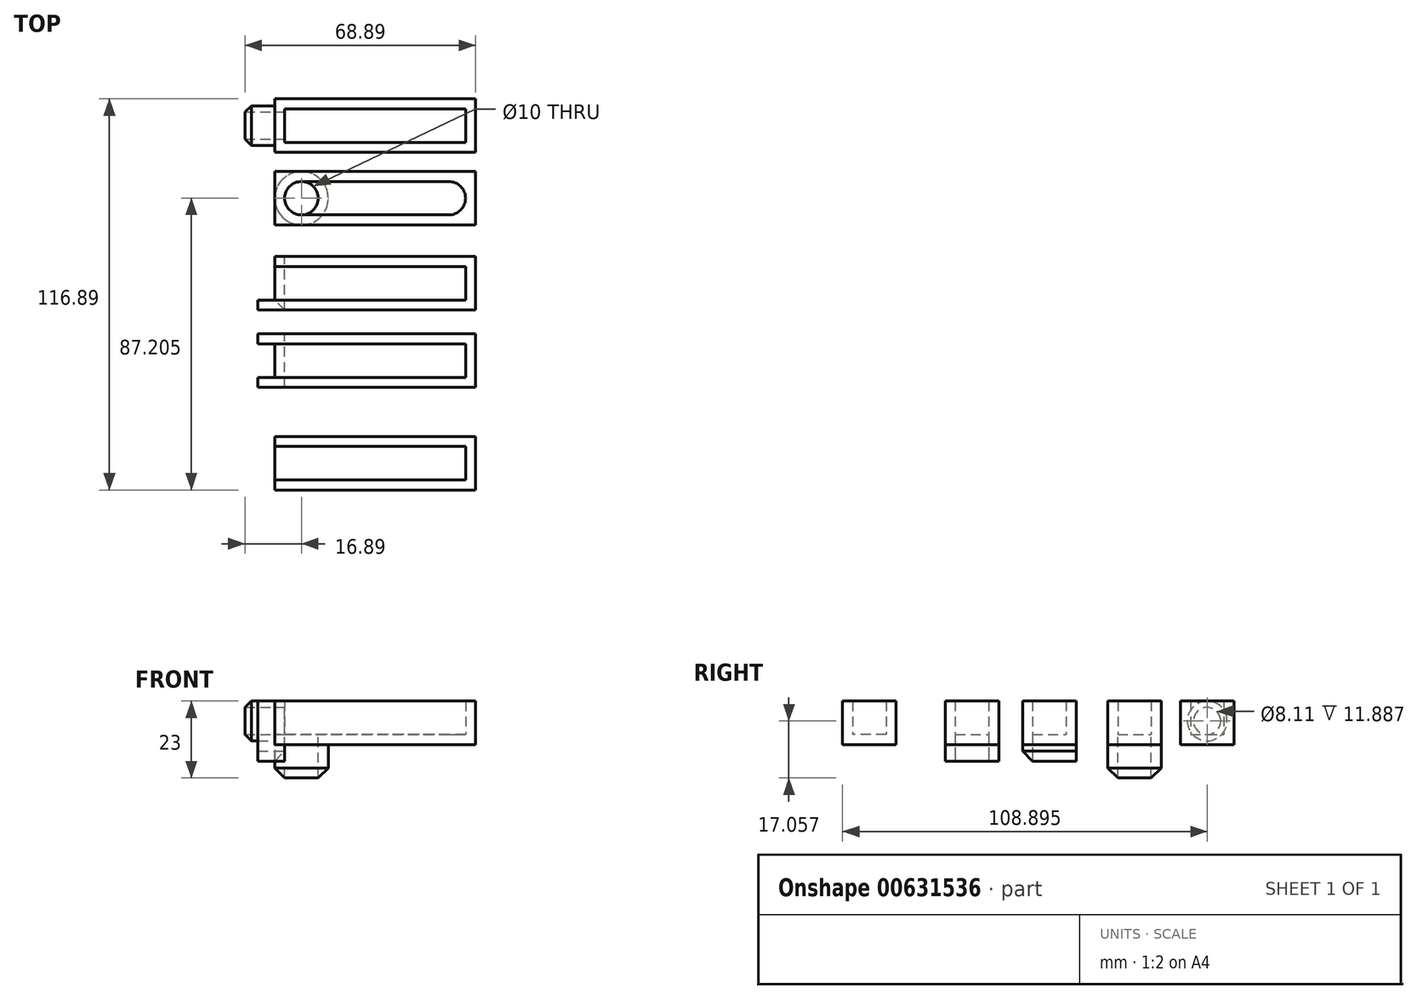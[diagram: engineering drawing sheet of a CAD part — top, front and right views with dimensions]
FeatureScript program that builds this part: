
annotation { "Feature Type Name" : "Feature", "Feature Type Description" : "" }
export const myFeature = defineFeature(function(context is Context, id is Id, definition is map)
    precondition{}
    {
        {
            var Q0;
            Q0=qCreatedBy(makeId("Top.planeOp"),FACE);
            var sketch = newSketch(context, id + "F0", { "sketchPlane" : qUnion([Q0])});
            skLineSegment(sketch, "E0.bottom", {"start": v(-30, 8) * mm, "end": v(30, 8) * mm});
            skLineSegment(sketch, "E0.top", {"start": v(-30, -8) * mm, "end": v(30, -8) * mm});
            skLineSegment(sketch, "E0.left", {"start": v(-30, 8) * mm, "end": v(-30, -8) * mm});
            skLineSegment(sketch, "E0.right", {"start": v(30, 8) * mm, "end": v(30, -8) * mm});
            skPoint(sketch, "E0.middle", {"position": v(0, 0) * mm});
            skLineSegment(sketch, "E1", {"start": v(-30, 5) * mm, "end": v(27, 5) * mm});
            skLineSegment(sketch, "E2", {"start": v(27, 5) * mm, "end": v(27, -5) * mm});
            skLineSegment(sketch, "E3", {"start": v(27, -5) * mm, "end": v(-30, -5) * mm});
            skLineSegment(sketch, "E4.bottom", {"start": v(-30, 22.66) * mm, "end": v(30, 22.66) * mm});
            skLineSegment(sketch, "E4.top", {"start": v(-30, 38.66) * mm, "end": v(30, 38.66) * mm});
            skLineSegment(sketch, "E4.left", {"start": v(-30, 22.66) * mm, "end": v(-30, 38.66) * mm});
            skLineSegment(sketch, "E4.right", {"start": v(30, 22.66) * mm, "end": v(30, 38.66) * mm});
            skLineSegment(sketch, "E5.bottom", {"start": v(-30, 45.78) * mm, "end": v(30, 45.78) * mm});
            skLineSegment(sketch, "E5.top", {"start": v(-30, 61.78) * mm, "end": v(30, 61.78) * mm});
            skLineSegment(sketch, "E5.left", {"start": v(-30, 45.78) * mm, "end": v(-30, 61.78) * mm});
            skLineSegment(sketch, "E5.right", {"start": v(30, 45.78) * mm, "end": v(30, 61.78) * mm});
            skLineSegment(sketch, "E6.bottom", {"start": v(27, 35.66) * mm, "end": v(-30, 35.66) * mm});
            skLineSegment(sketch, "E6.top", {"start": v(27, 25.66) * mm, "end": v(-30, 25.66) * mm});
            skLineSegment(sketch, "E6.left", {"start": v(27, 35.66) * mm, "end": v(27, 25.66) * mm});
            skLineSegment(sketch, "E6.right", {"start": v(-30, 35.66) * mm, "end": v(-30, 25.66) * mm});
            skLineSegment(sketch, "E7.bottom", {"start": v(27, 58.78) * mm, "end": v(-30, 58.78) * mm});
            skLineSegment(sketch, "E7.top", {"start": v(27, 48.78) * mm, "end": v(-30, 48.78) * mm});
            skLineSegment(sketch, "E7.left", {"start": v(27, 58.78) * mm, "end": v(27, 48.78) * mm});
            skLineSegment(sketch, "E7.right", {"start": v(-30, 58.78) * mm, "end": v(-30, 48.78) * mm});
            skLineSegment(sketch, "E8.bottom", {"start": v(-30, 71.2) * mm, "end": v(30, 71.2) * mm});
            skLineSegment(sketch, "E8.top", {"start": v(-30, 87.2) * mm, "end": v(30, 87.2) * mm});
            skLineSegment(sketch, "E8.left", {"start": v(-30, 71.2) * mm, "end": v(-30, 87.2) * mm});
            skLineSegment(sketch, "E8.right", {"start": v(30, 71.2) * mm, "end": v(30, 87.2) * mm});
            skLineSegment(sketch, "E9.bottom", {"start": v(-30, 92.9) * mm, "end": v(30, 92.9) * mm});
            skLineSegment(sketch, "E9.top", {"start": v(-30, 108.9) * mm, "end": v(30, 108.9) * mm});
            skLineSegment(sketch, "E9.left", {"start": v(-30, 92.9) * mm, "end": v(-30, 108.9) * mm});
            skLineSegment(sketch, "E9.right", {"start": v(30, 92.9) * mm, "end": v(30, 108.9) * mm});
            skLineSegment(sketch, "E10.bottom", {"start": v(22, 84.2) * mm, "end": v(-22, 84.2) * mm});
            skLineSegment(sketch, "E10.top", {"start": v(22, 74.2) * mm, "end": v(-22, 74.2) * mm});
            skLineSegment(sketch, "E10.left", {"start": v(27, 79.2) * mm, "end": v(27, 79.2) * mm});
            skLineSegment(sketch, "E10.right", {"start": v(-27, 79.2) * mm, "end": v(-27, 79.2) * mm});
            skLineSegment(sketch, "E11.bottom", {"start": v(-27, 95.9) * mm, "end": v(27, 95.9) * mm});
            skLineSegment(sketch, "E11.top", {"start": v(-27, 105.9) * mm, "end": v(27, 105.9) * mm});
            skLineSegment(sketch, "E11.left", {"start": v(-27, 95.9) * mm, "end": v(-27, 105.9) * mm});
            skLineSegment(sketch, "E11.right", {"start": v(27, 95.9) * mm, "end": v(27, 105.9) * mm});
            skPoint(sketch, "E12.visualSharp", {"position": v(27, 84.2) * mm});
            skArc(sketch, "E12.filletArc", {"start": v(27, 79.2) * mm, "mid": v(25.54, 82.74) * mm, "end": v(22, 84.2) * mm});
            skPoint(sketch, "E13.visualSharp", {"position": v(27, 74.2) * mm});
            skArc(sketch, "E13.filletArc", {"start": v(22, 74.2) * mm, "mid": v(25.54, 75.67) * mm, "end": v(27, 79.2) * mm});
            skPoint(sketch, "E14.visualSharp", {"position": v(-27, 84.2) * mm});
            skArc(sketch, "E14.filletArc", {"start": v(-22, 84.2) * mm, "mid": v(-25.54, 82.74) * mm, "end": v(-27, 79.2) * mm});
            skPoint(sketch, "E15.visualSharp", {"position": v(-27, 74.2) * mm});
            skArc(sketch, "E15.filletArc", {"start": v(-27, 79.2) * mm, "mid": v(-25.54, 75.67) * mm, "end": v(-22, 74.2) * mm});
            skCircle(sketch, "E16", {"center": v(-22, 79.2) * mm, "radius": 5 * mm});
            skSolve(sketch);
        }
        {
            var Q0;
            {var subQ0=sQuery(id+"F0.wireOp",EDGE,"E1");Q0=makeQuery(id+"F0.imprint","IMPRINT",FACE,{"disambiguationData":[TD([[makeQuery(id+"F0.imprint","IMPRINT",EDGE,{"derivedFrom":subQ0}),-1.0]])]});}
            var Q1;
            {var subQ3=sQuery(id+"F0.wireOp",EDGE,"E0.bottom");Q1=makeQuery(id+"F0.imprint","IMPRINT",FACE,{"disambiguationData":[TD([[makeQuery(id+"F0.imprint","IMPRINT",EDGE,{"derivedFrom":subQ3}),-1.0]])]});}
            var Q2;
            {var subQ4=sQuery(id+"F0.wireOp",EDGE,"E4.bottom");Q2=makeQuery(id+"F0.imprint","IMPRINT",FACE,{"disambiguationData":[TD([[makeQuery(id+"F0.imprint","IMPRINT",EDGE,{"derivedFrom":subQ4}),1.0]])]});}
            var Q3;
            Q3=makeQuery(id+"F0.imprint","IMPRINT",FACE,{"disambiguationData":[TD([[makeQuery(id+"F0.imprint","IMPRINT",EDGE,{"derivedFrom":sQuery(id+"F0.wireOp",EDGE,"E6.bottom")}),1.0]])]});
            var Q4;
            {var subQ4=sQuery(id+"F0.wireOp",EDGE,"E5.bottom");Q4=makeQuery(id+"F0.imprint","IMPRINT",FACE,{"disambiguationData":[TD([[makeQuery(id+"F0.imprint","IMPRINT",EDGE,{"derivedFrom":subQ4}),1.0]])]});}
            var Q5;
            Q5=makeQuery(id+"F0.imprint","IMPRINT",FACE,{"disambiguationData":[TD([[makeQuery(id+"F0.imprint","IMPRINT",EDGE,{"derivedFrom":sQuery(id+"F0.wireOp",EDGE,"E7.bottom")}),1.0]])]});
            var Q6;
            Q6=makeQuery(id+"F0.imprint","IMPRINT",FACE,{"disambiguationData":[TD([[makeQuery(id+"F0.imprint","IMPRINT",EDGE,{"derivedFrom":sQuery(id+"F0.wireOp",EDGE,"E8.bottom")}),1.0]])]});
            var Q7;
            {var subQ1=sQuery(id+"F0.wireOp",EDGE,"E10.bottom");Q7=makeQuery(id+"F0.imprint","IMPRINT",FACE,{"disambiguationData":[TD([[makeQuery(id+"F0.imprint","IMPRINT",EDGE,{"derivedFrom":subQ1}),1.0]])]});}
            var Q8;
            Q8=makeQuery(id+"F0.imprint","IMPRINT",FACE,{"disambiguationData":[TD([[makeQuery(id+"F0.imprint","IMPRINT",EDGE,{"derivedFrom":sQuery(id+"F0.wireOp",EDGE,"E9.bottom")}),1.0]])]});
            var Q9;
            Q9=makeQuery(id+"F0.imprint","IMPRINT",FACE,{"disambiguationData":[TD([[makeQuery(id+"F0.imprint","IMPRINT",EDGE,{"derivedFrom":sQuery(id+"F0.wireOp",EDGE,"E11.bottom")}),1.0]])]});
            extrude(context, id + "F1", {"entities" : qUnion([Q0, Q1, Q2, Q3, Q4, Q5, Q6, Q7, Q8, Q9]), "oppositeDirection" : true, "depth" : 3 * mm, "offsetDistance" : 25 * mm});
        }
        {
            var Q0;
            {var subQ3=sQuery(id+"F0.wireOp",EDGE,"E0.bottom");Q0=makeQuery(id+"F0.imprint","IMPRINT",FACE,{"disambiguationData":[TD([[makeQuery(id+"F0.imprint","IMPRINT",EDGE,{"derivedFrom":subQ3}),-1.0]])]});}
            extrude(context, id + "F2", {"entities" : qUnion([Q0]), "operationType" : NewBodyOperationType.ADD, "depth" : 10 * mm, "offsetDistance" : 25 * mm});
        }
        {
            var Q0;
            {var subQ4=sQuery(id+"F0.wireOp",EDGE,"E4.bottom");Q0=makeQuery(id+"F0.imprint","IMPRINT",FACE,{"disambiguationData":[TD([[makeQuery(id+"F0.imprint","IMPRINT",EDGE,{"derivedFrom":subQ4}),1.0]])]});}
            extrude(context, id + "F3", {"entities" : qUnion([Q0]), "operationType" : NewBodyOperationType.ADD, "depth" : 10 * mm, "offsetDistance" : 25 * mm});
        }
        {
            var Q0;
            {var subQ4=sQuery(id+"F0.wireOp",EDGE,"E5.bottom");Q0=makeQuery(id+"F0.imprint","IMPRINT",FACE,{"disambiguationData":[TD([[makeQuery(id+"F0.imprint","IMPRINT",EDGE,{"derivedFrom":subQ4}),1.0]])]});}
            extrude(context, id + "F4", {"entities" : qUnion([Q0]), "operationType" : NewBodyOperationType.ADD, "depth" : 10 * mm, "offsetDistance" : 25 * mm});
        }
        {
            var Q0;
            Q0=makeQuery(id+"F0.imprint","IMPRINT",FACE,{"disambiguationData":[TD([[makeQuery(id+"F0.imprint","IMPRINT",EDGE,{"derivedFrom":sQuery(id+"F0.wireOp",EDGE,"E8.bottom")}),1.0]])]});
            extrude(context, id + "F5", {"entities" : qUnion([Q0]), "operationType" : NewBodyOperationType.ADD, "depth" : 10 * mm, "offsetDistance" : 25 * mm});
        }
        {
            var Q0;
            Q0=makeQuery(id+"F0.imprint","IMPRINT",FACE,{"disambiguationData":[TD([[makeQuery(id+"F0.imprint","IMPRINT",EDGE,{"derivedFrom":sQuery(id+"F0.wireOp",EDGE,"E9.bottom")}),1.0]])]});
            extrude(context, id + "F6", {"entities" : qUnion([Q0]), "operationType" : NewBodyOperationType.ADD, "depth" : 10 * mm, "offsetDistance" : 25 * mm});
        }
        {
            var Q0;
            Q0=makeQuery(id+"F1.opExtrude","CAP_FACE",FACE,{"disambiguationData":[OSD([sQuery(id+"F0.wireOp",EDGE,"E4.bottom"),sQuery(id+"F0.wireOp",EDGE,"E4.top"),sQuery(id+"F0.wireOp",EDGE,"E4.left"),sQuery(id+"F0.wireOp",EDGE,"E4.right"),sQuery(id+"F0.wireOp",EDGE,"E6.right")])],"isStart":false});
            var sketch = newSketch(context, id + "F7", { "sketchPlane" : qUnion([Q0])});
            skLineSegment(sketch, "E17.0", {"start": v(-30, -22.66) * mm, "end": v(-30, -38.66) * mm});
            skLineSegment(sketch, "E18.0", {"start": v(-30, -45.78) * mm, "end": v(-30, -61.78) * mm});
            skCircle(sketch, "E19.0", {"center": v(-22, -79.2) * mm, "radius": 5 * mm});
            skLineSegment(sketch, "E20.bottom", {"start": v(-30, -22.66) * mm, "end": v(-27, -22.66) * mm});
            skLineSegment(sketch, "E20.top", {"start": v(-30, -38.66) * mm, "end": v(-27, -38.66) * mm});
            skLineSegment(sketch, "E20.right", {"start": v(-27, -22.66) * mm, "end": v(-27, -38.66) * mm});
            skLineSegment(sketch, "E21.bottom", {"start": v(-30, -45.78) * mm, "end": v(-27, -45.78) * mm});
            skLineSegment(sketch, "E21.top", {"start": v(-30, -61.78) * mm, "end": v(-27, -61.78) * mm});
            skLineSegment(sketch, "E21.right", {"start": v(-27, -45.78) * mm, "end": v(-27, -61.78) * mm});
            skCircle(sketch, "E22", {"center": v(-22, -79.2) * mm, "radius": 8 * mm});
            skSolve(sketch);
        }
        {
            var Q0;
            Q0=makeQuery(id+"F7.imprint","IMPRINT",FACE,{"disambiguationData":[TD([[makeQuery(id+"F7.imprint","IMPRINT",EDGE,{"derivedFrom":sQuery(id+"F7.wireOp",EDGE,"E20.bottom")}),-1.0]])]});
            extrude(context, id + "F8", {"entities" : qUnion([Q0]), "operationType" : NewBodyOperationType.ADD, "depth" : 5 * mm, "offsetDistance" : 25 * mm});
        }
        {
            var Q0;
            Q0=makeQuery(id+"F7.imprint","IMPRINT",FACE,{"disambiguationData":[TD([[makeQuery(id+"F7.imprint","IMPRINT",EDGE,{"derivedFrom":sQuery(id+"F7.wireOp",EDGE,"E21.bottom")}),-1.0]])]});
            extrude(context, id + "F9", {"entities" : qUnion([Q0]), "operationType" : NewBodyOperationType.ADD, "depth" : 5 * mm, "offsetDistance" : 25 * mm});
        }
        {
            var Q0;
            Q0=makeQuery(id+"F7.imprint","IMPRINT",FACE,{"disambiguationData":[TD([[makeQuery(id+"F7.imprint","IMPRINT",EDGE,{"derivedFrom":sQuery(id+"F7.wireOp",EDGE,"E19.0")}),-1.0]])]});
            extrude(context, id + "F10", {"entities" : qUnion([Q0]), "operationType" : NewBodyOperationType.ADD, "depth" : 10 * mm, "offsetDistance" : 25 * mm});
        }
        {
            var Q0;
            {var subQ0=sQuery(id+"F0.wireOp",EDGE,"E4.left");var subQ1=sQuery(id+"F0.wireOp",EDGE,"E6.right");Q0=makeQuery(id+"F8.boolean.opBoolean","MERGE",FACE,{"derivedFrom":[makeQuery(id+"F3.boolean.opBoolean","MERGE",FACE,{"derivedFrom":[makeQuery(id+"F1.opExtrude","SWEPT_FACE",FACE,{"disambiguationData":[OSD([subQ0,subQ1])]}),makeQuery(id+"F3.opExtrude","SWEPT_FACE",FACE,{"disambiguationData":[OSD([subQ0]),TDD([makeQuery(id+"F0.imprint","IMPRINT",EDGE,{"disambiguationData":[TD([[makeQuery(id+"F0.imprint","INTERSECT",VERTEX,{"derivedFrom":[sQuery(id+"F0.wireOp",EDGE,"E4.bottom"),subQ0]}),-1.0]])],"derivedFrom":subQ0})])]}),makeQuery(id+"F3.opExtrude","SWEPT_FACE",FACE,{"disambiguationData":[OSD([subQ0]),TDD([makeQuery(id+"F0.imprint","IMPRINT",EDGE,{"disambiguationData":[TD([[makeQuery(id+"F0.imprint","INTERSECT",VERTEX,{"derivedFrom":[sQuery(id+"F0.wireOp",EDGE,"E4.top"),subQ0]}),1.0]])],"derivedFrom":subQ0})])]})]}),makeQuery(id+"F8.opExtrude","SWEPT_FACE",FACE,{"disambiguationData":[OSD([sQuery(id+"F7.wireOp",EDGE,"E17.0")])]})]});}
            var sketch = newSketch(context, id + "F11", { "sketchPlane" : qUnion([Q0])});
            skLineSegment(sketch, "E23.0", {"start": v(-25.66, 10) * mm, "end": v(-25.66, 0) * mm});
            skLineSegment(sketch, "E24.0", {"start": v(-35.66, 10) * mm, "end": v(-35.66, 0) * mm});
            skLineSegment(sketch, "E25.0", {"start": v(-35.66, 10) * mm, "end": v(-38.66, 10) * mm});
            skLineSegment(sketch, "E26.0", {"start": v(-22.66, 10) * mm, "end": v(-25.66, 10) * mm});
            skLineSegment(sketch, "E27.0", {"start": v(-45.78, 10) * mm, "end": v(-48.78, 10) * mm});
            skLineSegment(sketch, "E28.0", {"start": v(-48.78, 10) * mm, "end": v(-48.78, 0) * mm});
            skLineSegment(sketch, "E29.0", {"start": v(-58.78, 10) * mm, "end": v(-58.78, 0) * mm});
            skLineSegment(sketch, "E30.0", {"start": v(-58.78, 10) * mm, "end": v(-61.78, 10) * mm});
            skPoint(sketch, "E31.0", {"position": v(-61.78, -8) * mm});
            skPoint(sketch, "E32.0", {"position": v(-45.78, -8) * mm});
            skPoint(sketch, "E33.0", {"position": v(-38.66, -8) * mm});
            skLineSegment(sketch, "E34.0", {"start": v(-22.66, -8) * mm, "end": v(-22.66, 10) * mm});
            skLineSegment(sketch, "E35", {"start": v(-38.66, 10) * mm, "end": v(-38.66, -8) * mm});
            skLineSegment(sketch, "E36", {"start": v(-35.66, 0) * mm, "end": v(-35.66, -8) * mm});
            skLineSegment(sketch, "E37", {"start": v(-35.66, -8) * mm, "end": v(-38.66, -8) * mm});
            skLineSegment(sketch, "E38", {"start": v(-25.66, 0) * mm, "end": v(-25.66, -8) * mm});
            skLineSegment(sketch, "E39", {"start": v(-25.66, -8) * mm, "end": v(-22.66, -8) * mm});
            skLineSegment(sketch, "E40", {"start": v(-48.78, 0) * mm, "end": v(-48.78, -8) * mm});
            skLineSegment(sketch, "E41.bottom", {"start": v(-61.78, 10) * mm, "end": v(-58.78, 10) * mm});
            skLineSegment(sketch, "E41.top", {"start": v(-61.78, -8) * mm, "end": v(-58.78, -8) * mm});
            skLineSegment(sketch, "E41.left", {"start": v(-61.78, 10) * mm, "end": v(-61.78, -8) * mm});
            skLineSegment(sketch, "E41.right", {"start": v(-58.78, 10) * mm, "end": v(-58.78, -8) * mm});
            skLineSegment(sketch, "E42.0", {"start": v(-92.9, -3) * mm, "end": v(-92.9, 10) * mm});
            skLineSegment(sketch, "E43.0", {"start": v(-92.9, 10) * mm, "end": v(-108.9, 10) * mm});
            skCircle(sketch, "E44", {"center": v(-100.9, 4.06) * mm, "radius": 4.06 * mm});
            skPoint(sketch, "E44.centerSnap0", {"position": v(-100.9, 10) * mm});
            skCircle(sketch, "E45", {"center": v(-100.9, 4.06) * mm, "radius": 5.94 * mm});
            skLineSegment(sketch, "E46.bottom", {"start": v(-45.78, -8) * mm, "end": v(-48.78, -8) * mm});
            skLineSegment(sketch, "E46.left", {"start": v(-45.78, -8) * mm, "end": v(-45.78, 10) * mm});
            skLineSegment(sketch, "E46.right", {"start": v(-48.78, -8) * mm, "end": v(-48.78, 10) * mm});
            skLineSegment(sketch, "E47.bottom", {"start": v(-58.78, -8) * mm, "end": v(-61.78, -8) * mm});
            skLineSegment(sketch, "E47.left", {"start": v(-58.78, -8) * mm, "end": v(-58.78, 10) * mm});
            skLineSegment(sketch, "E47.right", {"start": v(-61.78, -8) * mm, "end": v(-61.78, 10) * mm});
            skSolve(sketch);
        }
        {
            var Q0;
            Q0=makeQuery(id+"F11.imprint","IMPRINT",FACE,{"disambiguationData":[TD([[makeQuery(id+"F11.imprint","IMPRINT",EDGE,{"derivedFrom":sQuery(id+"F11.wireOp",EDGE,"E24.0")}),-1.0]])]});
            var Q1;
            Q1=makeQuery(id+"F11.imprint","IMPRINT",FACE,{"disambiguationData":[TD([[makeQuery(id+"F11.imprint","IMPRINT",EDGE,{"derivedFrom":sQuery(id+"F11.wireOp",EDGE,"E23.0")}),1.0]])]});
            extrude(context, id + "F12", {"entities" : qUnion([Q0, Q1]), "operationType" : NewBodyOperationType.ADD, "depth" : 5 * mm, "offsetDistance" : 25 * mm});
        }
        {
            var Q0;
            Q0=makeQuery(id+"F11.imprint","IMPRINT",FACE,{"disambiguationData":[TD([[makeQuery(id+"F11.imprint","IMPRINT",EDGE,{"derivedFrom":sQuery(id+"F11.wireOp",EDGE,"E46.bottom")}),-1.0]])]});
            var Q1;
            {var subQ3=sQuery(id+"F11.wireOp",EDGE,"E47.bottom");Q1=makeQuery(id+"F11.imprint","IMPRINT",FACE,{"disambiguationData":[TD([[makeQuery(id+"F11.imprint","IMPRINT",EDGE,{"derivedFrom":subQ3}),-1.0]])]});}
            extrude(context, id + "F13", {"entities" : qUnion([Q0, Q1]), "operationType" : NewBodyOperationType.ADD, "depth" : 5 * mm, "offsetDistance" : 25 * mm});
        }
        {
            var Q0;
            Q0=makeQuery(id+"F11.imprint","IMPRINT",FACE,{"disambiguationData":[TD([[makeQuery(id+"F11.imprint","IMPRINT",EDGE,{"derivedFrom":sQuery(id+"F11.wireOp",EDGE,"E44")}),-1.0]])]});
            extrude(context, id + "F14", {"entities" : qUnion([Q0]), "operationType" : NewBodyOperationType.ADD, "depth" : 10 * mm, "offsetDistance" : 25 * mm});
        }
        {
            var Q0;
            Q0=makeQuery(id+"F11.imprint","IMPRINT",FACE,{"disambiguationData":[TD([[makeQuery(id+"F11.imprint","IMPRINT",EDGE,{"derivedFrom":sQuery(id+"F11.wireOp",EDGE,"E44")}),1.0]])]});
            extrude(context, id + "F15", {"entities" : qUnion([Q0]), "operationType" : NewBodyOperationType.REMOVE, "oppositeDirection" : true, "depth" : 25 * mm, "offsetDistance" : 25 * mm});
        }
        {
            var Q0;
            Q0=makeQuery(id+"F9.opExtrude","CAP_EDGE",EDGE,{"disambiguationData":[OSD([sQuery(id+"F7.wireOp",EDGE,"E21.right")])],"isStart":false});
            var Q1;
            Q1=makeQuery(id+"F13.boolean.opBoolean","MERGE",EDGE,{"derivedFrom":[makeQuery(id+"F9.opExtrude","CAP_EDGE",EDGE,{"disambiguationData":[OSD([sQuery(id+"F7.wireOp",EDGE,"E21.bottom")])],"isStart":false}),makeQuery(id+"F13.opExtrude","SWEPT_EDGE",EDGE,{"disambiguationData":[OSD([sQuery(id+"F11.wireOp",EDGE,"E46.bottom"),sQuery(id+"F11.wireOp",EDGE,"E46.left")])]})]});
            var Q2;
            Q2=makeQuery(id+"F13.boolean.opBoolean","MERGE",EDGE,{"derivedFrom":[makeQuery(id+"F9.opExtrude","CAP_EDGE",EDGE,{"disambiguationData":[OSD([sQuery(id+"F7.wireOp",EDGE,"E21.top")])],"isStart":false}),makeQuery(id+"F13.opExtrude","SWEPT_EDGE",EDGE,{"disambiguationData":[OSD([sQuery(id+"F11.wireOp",EDGE,"E47.bottom"),sQuery(id+"F11.wireOp",EDGE,"E47.right")])]})]});
            chamfer(context, id + "F16", {"entities" : qUnion([Q0, Q1, Q2]), "width" : 3 * mm, "tangentPropagation" : true});
        }
        {
            var Q0;
            Q0=makeQuery(id+"F10.opExtrude","CAP_EDGE",EDGE,{"disambiguationData":[OSD([sQuery(id+"F7.wireOp",EDGE,"E22")])],"isStart":false});
            var Q1;
            Q1=makeQuery(id+"F14.opExtrude","CAP_EDGE",EDGE,{"disambiguationData":[OSD([sQuery(id+"F11.wireOp",EDGE,"E45")])],"isStart":false});
            chamfer(context, id + "F17", {"entities" : qUnion([Q0, Q1]), "width" : 3 * mm, "tangentPropagation" : true});
        }
    });
